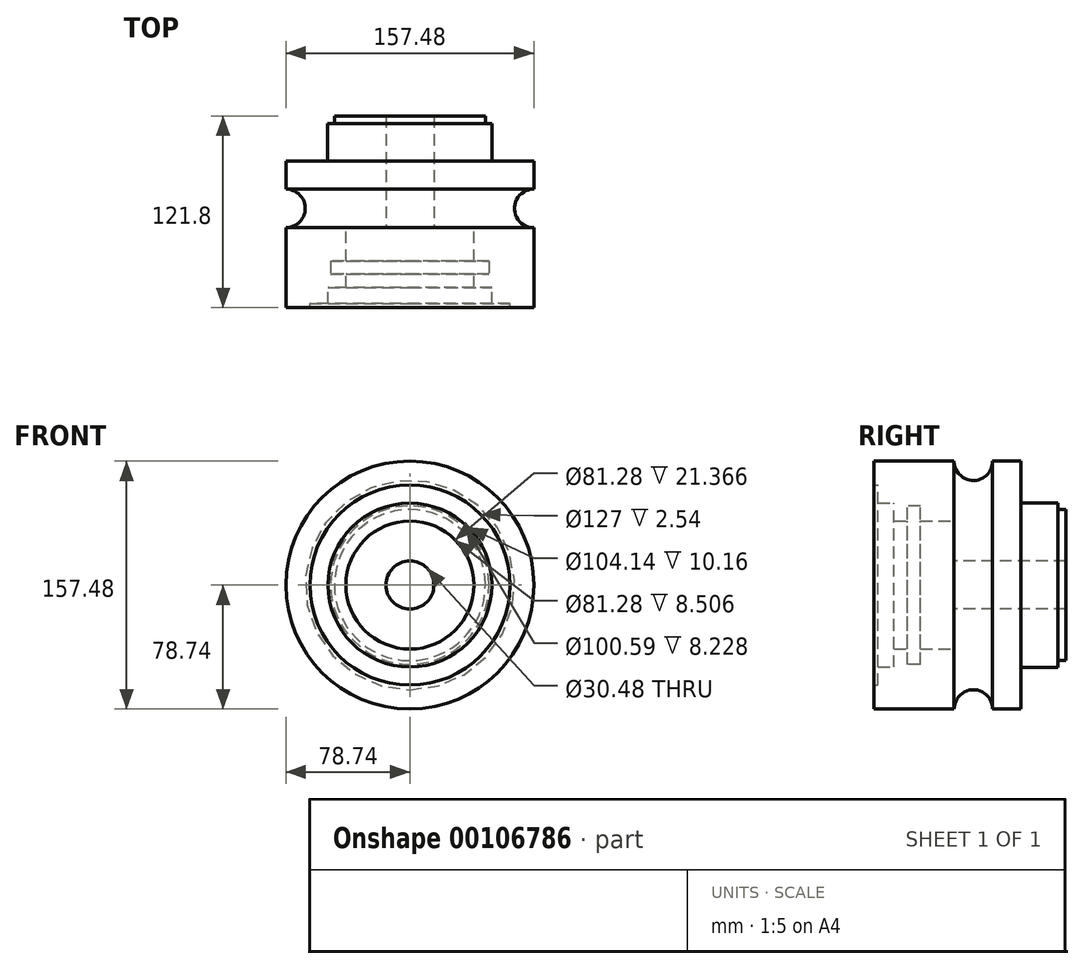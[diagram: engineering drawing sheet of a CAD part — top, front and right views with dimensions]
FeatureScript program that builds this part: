
annotation { "Feature Type Name" : "Feature", "Feature Type Description" : "" }
export const myFeature = defineFeature(function(context is Context, id is Id, definition is map)
    precondition{}
    {
        {
            var Q0;
            Q0=qCreatedBy(makeId("Front.planeOp"),FACE);
            var sketch = newSketch(context, id + "F0", { "sketchPlane" : qUnion([Q0])});
            skCircle(sketch, "E0", {"center": v(0, 0) * mm, "radius": 78.74 * mm});
            skCircle(sketch, "E1", {"center": v(0, 0) * mm, "radius": 63.5 * mm});
            skSolve(sketch);
        }
        {
            var Q0;
            Q0 = qSketchRegion(id + "F0", true);
            extrude(context, id + "F1", {"entities" : qUnion([Q0]), "depth" : 50.8 * mm});
        }
        {
            var Q0;
            Q0=qCreatedBy(makeId("Front.planeOp"),FACE);
            var sketch = newSketch(context, id + "F2", { "sketchPlane" : qUnion([Q0])});
            skCircle(sketch, "E2", {"center": v(0, 0) * mm, "radius": 52.07 * mm});
            skCircle(sketch, "E3", {"center": v(0, 0) * mm, "radius": 63.5 * mm});
            skSolve(sketch);
        }
        {
            var Q0;
            Q0=qCreatedBy(makeId("Right.planeOp"),FACE);
            var sketch = newSketch(context, id + "F3", { "sketchPlane" : qUnion([Q0])});
            skLineSegment(sketch, "E4.bottom", {"start": v(24.47, 78.7) * mm, "end": v(42.33, 78.7) * mm});
            skLineSegment(sketch, "E4.top", {"start": v(24.47, 1.87) * mm, "end": v(42.33, 1.87) * mm});
            skLineSegment(sketch, "E4.left", {"start": v(24.47, 78.7) * mm, "end": v(24.47, 1.87) * mm});
            skLineSegment(sketch, "E4.right", {"start": v(42.33, 78.7) * mm, "end": v(42.33, 1.87) * mm});
            skLineSegment(sketch, "E5", {"start": v(24.47, 1.87) * mm, "end": v(0, 1.87) * mm});
            skLineSegment(sketch, "E6", {"start": v(0, 1.87) * mm, "end": v(0, 78.7) * mm});
            skLineSegment(sketch, "E7.bottom", {"start": v(42.33, 1.87) * mm, "end": v(65.96, 1.87) * mm});
            skLineSegment(sketch, "E7.top", {"start": v(42.33, 52.15) * mm, "end": v(65.96, 52.15) * mm});
            skLineSegment(sketch, "E7.left", {"start": v(42.33, 1.87) * mm, "end": v(42.33, 52.15) * mm});
            skLineSegment(sketch, "E7.right", {"start": v(65.96, 1.87) * mm, "end": v(65.96, 52.15) * mm});
            skLineSegment(sketch, "E8.bottom", {"start": v(65.96, 1.87) * mm, "end": v(71, 1.87) * mm});
            skLineSegment(sketch, "E8.top", {"start": v(65.96, 47.96) * mm, "end": v(71, 47.96) * mm});
            skLineSegment(sketch, "E8.left", {"start": v(65.96, 1.87) * mm, "end": v(65.96, 47.96) * mm});
            skLineSegment(sketch, "E8.right", {"start": v(71, 1.87) * mm, "end": v(71, 47.96) * mm});
            skLineSegment(sketch, "E9", {"start": v(0, 0) * mm, "end": v(47.06, 0) * mm, "construction": true});
            skArc(sketch, "E10", {"start": v(0, 78.7) * mm, "mid": v(12.24, 66.46) * mm, "end": v(24.47, 78.7) * mm});
            skSolve(sketch);
        }
        {
            var Q0;
            Q0=qCreatedBy(makeId("Front.planeOp"),FACE);
            var sketch = newSketch(context, id + "F4", { "sketchPlane" : qUnion([Q0])});
            skCircle(sketch, "E11", {"center": v(0, 0) * mm, "radius": 40.64 * mm});
            skCircle(sketch, "E12", {"center": v(0, 0) * mm, "radius": 63.5 * mm});
            skSolve(sketch);
        }
        {
            var Q0;
            Q0 = qSketchRegion(id + "F2", true);
            extrude(context, id + "F5", {"entities" : qUnion([Q0]), "operationType" : NewBodyOperationType.ADD, "depth" : 48.26 * mm});
        }
        {
            var Q0;
            Q0 = qSketchRegion(id + "F4", true);
            extrude(context, id + "F6", {"entities" : qUnion([Q0]), "operationType" : NewBodyOperationType.ADD, "depth" : 38.1 * mm});
        }
        {
            var Q0;
            Q0 = qSketchRegion(id + "F3", true);
            var Q1;
            Q1=sQuery(id+"F3.wireOp",EDGE,"E9");
            revolve(context, id + "F7", {"operationType" : NewBodyOperationType.ADD, "entities" : qUnion([Q0]), "axis" : qUnion([Q1]), "revolveType" : RevolveType.FULL});
        }
        {
            var Q0;
            Q0=qCreatedBy(makeId("Right.planeOp"),FACE);
            var sketch = newSketch(context, id + "F8", { "sketchPlane" : qUnion([Q0])});
            skLineSegment(sketch, "E13", {"start": v(0, 0) * mm, "end": v(-50.83, 0) * mm});
            skLineSegment(sketch, "E14.bottom", {"start": v(-29.6, 6.24) * mm, "end": v(-21.37, 6.24) * mm});
            skLineSegment(sketch, "E14.top", {"start": v(-29.6, 50.3) * mm, "end": v(-21.37, 50.3) * mm});
            skLineSegment(sketch, "E14.left", {"start": v(-29.6, 6.24) * mm, "end": v(-29.6, 50.3) * mm});
            skLineSegment(sketch, "E14.right", {"start": v(-21.37, 6.24) * mm, "end": v(-21.37, 50.3) * mm});
            skLineSegment(sketch, "E15.bottom", {"start": v(-29.6, 39.68) * mm, "end": v(-39.15, 39.68) * mm});
            skLineSegment(sketch, "E15.top", {"start": v(-29.6, 6.24) * mm, "end": v(-39.15, 6.24) * mm});
            skLineSegment(sketch, "E15.left", {"start": v(-29.6, 39.68) * mm, "end": v(-29.6, 6.24) * mm});
            skLineSegment(sketch, "E15.right", {"start": v(-39.15, 39.68) * mm, "end": v(-39.15, 6.24) * mm});
            skSolve(sketch);
        }
        {
            var Q0;
            Q0 = qSketchRegion(id + "F8", true);
            var Q1;
            Q1=sQuery(id+"F8.wireOp",EDGE,"E13");
            revolve(context, id + "F9", {"operationType" : NewBodyOperationType.REMOVE, "entities" : qUnion([Q0]), "axis" : qUnion([Q1]), "revolveType" : RevolveType.FULL, "oppositeDirection" : true});
        }
        {
            var Q0;
            Q0=qCreatedBy(makeId("Front.planeOp"),FACE);
            var sketch = newSketch(context, id + "F10", { "sketchPlane" : qUnion([Q0])});
            skCircle(sketch, "E16", {"center": v(0, 0) * mm, "radius": 15.24 * mm});
            skSolve(sketch);
        }
        {
            var Q0;
            Q0 = qSketchRegion(id + "F10", true);
            extrude(context, id + "F11", {"entities" : qUnion([Q0]), "operationType" : NewBodyOperationType.REMOVE, "endBound" : BoundingType.THROUGH_ALL, "oppositeDirection" : true, "depth" : 25.4 * mm});
        }
    });
